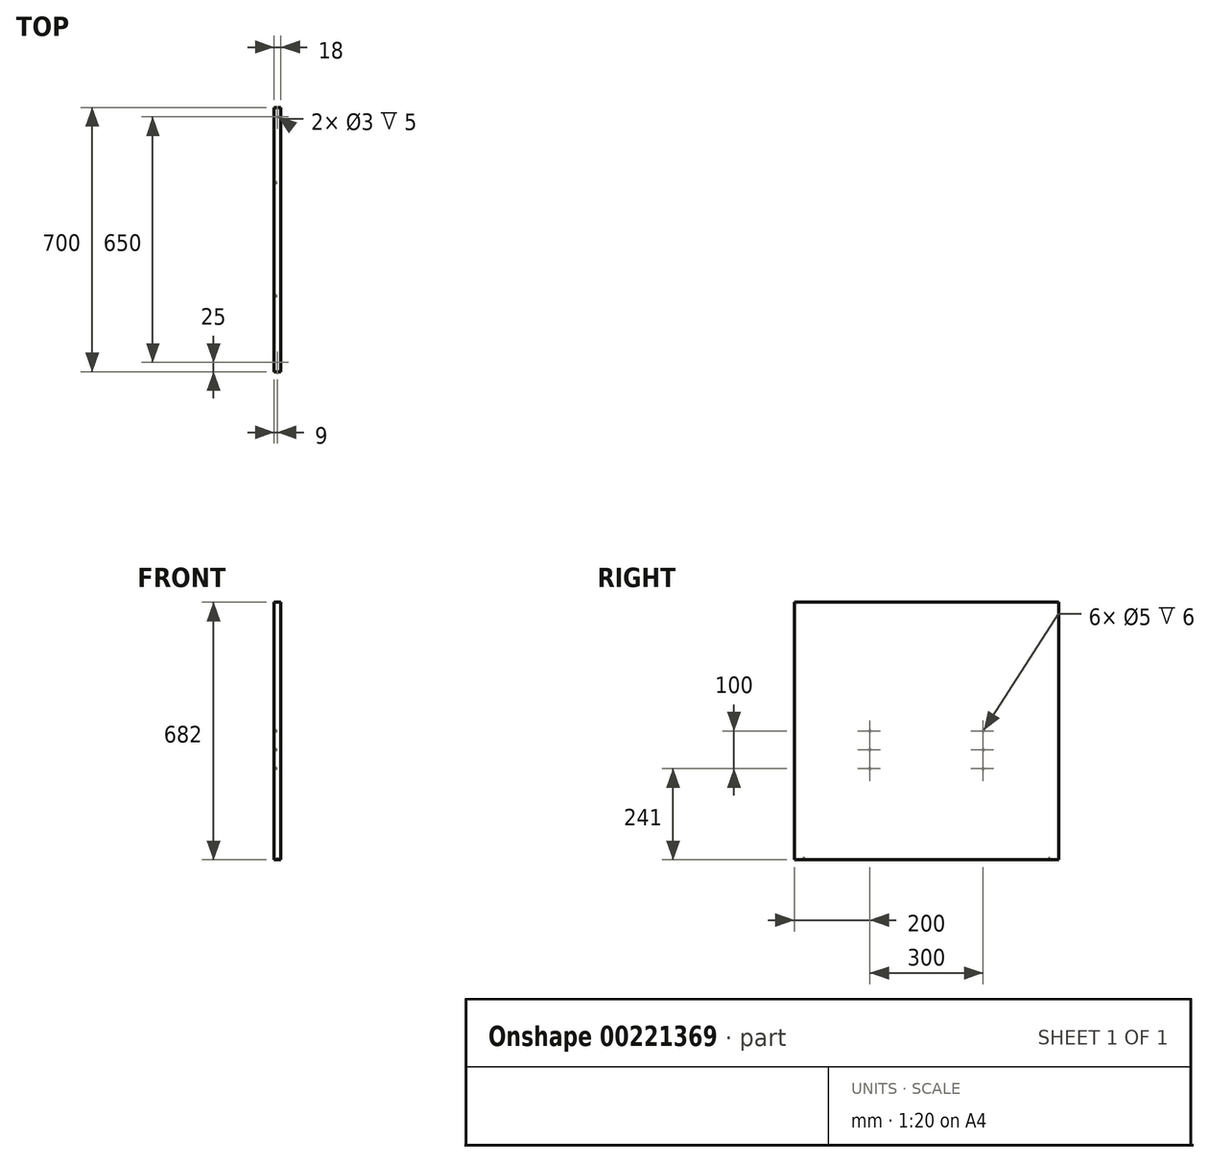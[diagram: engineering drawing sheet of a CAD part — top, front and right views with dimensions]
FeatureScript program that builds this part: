
annotation { "Feature Type Name" : "Feature", "Feature Type Description" : "" }
export const myFeature = defineFeature(function(context is Context, id is Id, definition is map)
    precondition{}
    {
        {
            var Q0;
            Q0=qCreatedBy(makeId("Right.planeOp"),FACE);
            var sketch = newSketch(context, id + "F0", { "sketchPlane" : qUnion([Q0])});
            skLineSegment(sketch, "E0.bottom", {"start": v(350, -341) * mm, "end": v(-350, -341) * mm});
            skLineSegment(sketch, "E0.top", {"start": v(350, 341) * mm, "end": v(-350, 341) * mm});
            skLineSegment(sketch, "E0.left", {"start": v(350, -341) * mm, "end": v(350, 341) * mm});
            skLineSegment(sketch, "E0.right", {"start": v(-350, -341) * mm, "end": v(-350, 341) * mm});
            skPoint(sketch, "E0.middle", {"position": v(0, 0) * mm});
            skSolve(sketch);
        }
        {
            var Q0;
            Q0 = qSketchRegion(id + "F0", true);
            extrude(context, id + "F1", {"entities" : qUnion([Q0]), "depth" : 18 * mm});
        }
        {
            var Q0;
            Q0=makeQuery(id+"F1.opExtrude","SWEPT_FACE",FACE,{"disambiguationData":[OSD([sQuery(id+"F0.wireOp",EDGE,"E0.bottom")])]});
            var sketch = newSketch(context, id + "F2", { "sketchPlane" : qUnion([Q0])});
            skCircle(sketch, "E1", {"center": v(9, 325) * mm, "radius": 1.5 * mm});
            skCircle(sketch, "E2", {"center": v(9, -325) * mm, "radius": 1.5 * mm});
            skSolve(sketch);
        }
        {
            var Q0;
            Q0 = qSketchRegion(id + "F2", true);
            extrude(context, id + "F3", {"entities" : qUnion([Q0]), "operationType" : NewBodyOperationType.REMOVE, "oppositeDirection" : true, "depth" : 5 * mm});
        }
        {
            var Q0;
            Q0=makeQuery(id+"F1.opExtrude","CAP_FACE",FACE,{"disambiguationData":[OSD([sQuery(id+"F0.wireOp",EDGE,"E0.bottom"),sQuery(id+"F0.wireOp",EDGE,"E0.top"),sQuery(id+"F0.wireOp",EDGE,"E0.left"),sQuery(id+"F0.wireOp",EDGE,"E0.right")])],"isStart":true});
            var sketch = newSketch(context, id + "F4", { "sketchPlane" : qUnion([Q0])});
            skCircle(sketch, "E3", {"center": v(-150, 0) * mm, "radius": 2.5 * mm});
            skCircle(sketch, "E4", {"center": v(150, 0) * mm, "radius": 2.5 * mm});
            skCircle(sketch, "E5.0.1.0", {"center": v(-150, -50) * mm, "radius": 2.5 * mm});
            skCircle(sketch, "E5.0.1.1", {"center": v(150, -50) * mm, "radius": 2.5 * mm});
            skCircle(sketch, "E5.0.2.0", {"center": v(-150, -100) * mm, "radius": 2.5 * mm});
            skCircle(sketch, "E5.0.2.1", {"center": v(150, -100) * mm, "radius": 2.5 * mm});
            skLineSegment(sketch, "E5.direction1", {"start": v(-150, 0) * mm, "end": v(-125, 0) * mm, "construction": true});
            skLineSegment(sketch, "E5.direction2", {"start": v(-150, 0) * mm, "end": v(-150, -50) * mm, "construction": true});
            skSolve(sketch);
        }
        {
            var Q0;
            Q0 = qSketchRegion(id + "F4", true);
            extrude(context, id + "F5", {"entities" : qUnion([Q0]), "operationType" : NewBodyOperationType.REMOVE, "oppositeDirection" : true, "depth" : 6 * mm});
        }
    });
